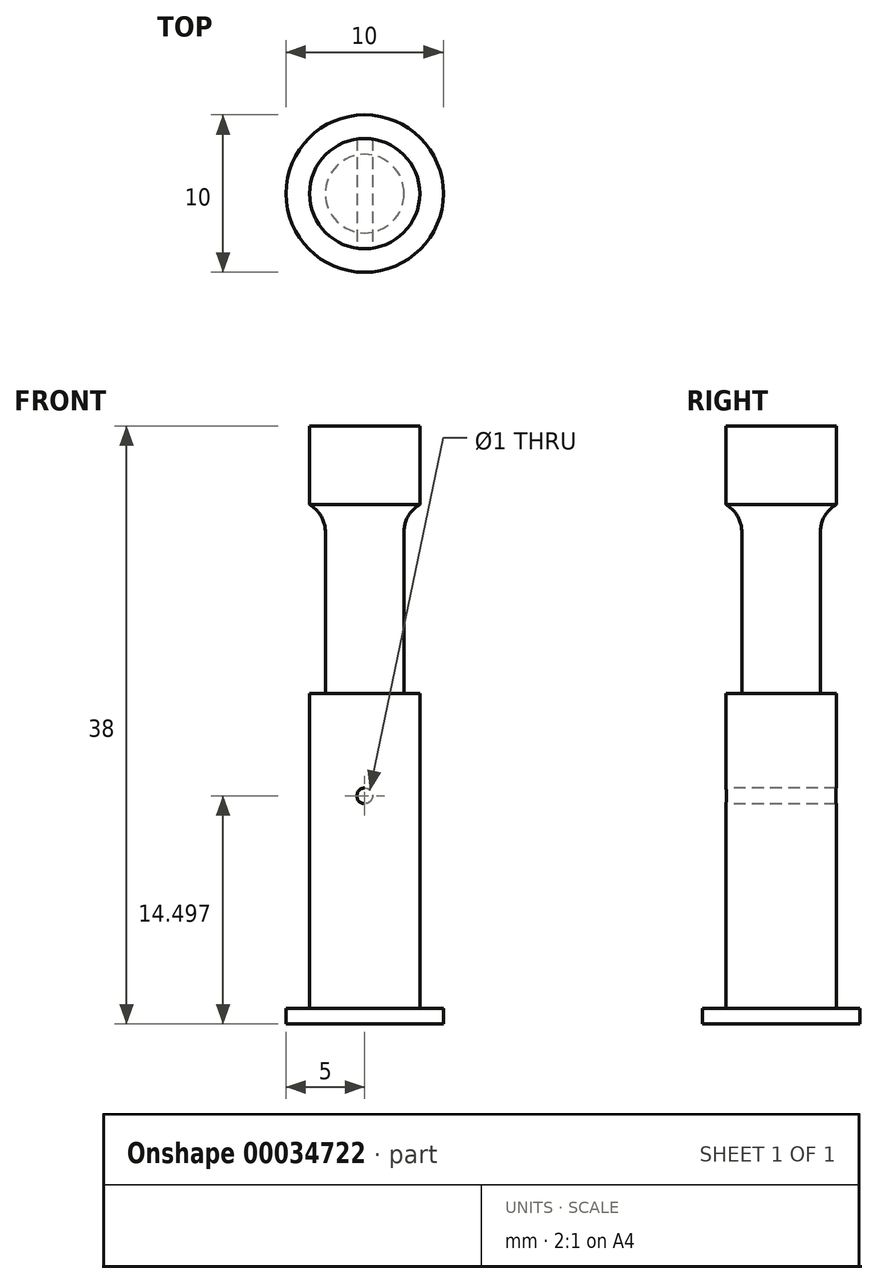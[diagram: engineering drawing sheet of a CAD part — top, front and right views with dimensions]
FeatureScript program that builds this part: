
annotation { "Feature Type Name" : "Feature", "Feature Type Description" : "" }
export const myFeature = defineFeature(function(context is Context, id is Id, definition is map)
    precondition{}
    {
        {
            var Q0;
            Q0=qCreatedBy(makeId("Top.planeOp"),FACE);
            var sketch = newSketch(context, id + "F0", { "sketchPlane" : qUnion([Q0])});
            skCircle(sketch, "E0", {"center": v(0, 0) * mm, "radius": 3.5 * mm});
            skCircle(sketch, "E1", {"center": v(0, 0) * mm, "radius": 5 * mm});
            skSolve(sketch);
        }
        {
            var Q0;
            Q0=makeQuery(id+"F0.imprint","IMPRINT",FACE,{"disambiguationData":[TD([[makeQuery(id+"F0.imprint","IMPRINT",EDGE,{"derivedFrom":sQuery(id+"F0.wireOp",EDGE,"E0")}),1.0]])]});
            extrude(context, id + "F1", {"entities" : qUnion([Q0]), "depth" : 13 * mm});
        }
        {
            var Q0;
            Q0=makeQuery(id+"F1.opExtrude","CAP_FACE",FACE,{"disambiguationData":[OSD([sQuery(id+"F0.wireOp",EDGE,"E0")])],"isStart":false});
            var sketch = newSketch(context, id + "F7", { "sketchPlane" : qUnion([Q0])});
            skCircle(sketch, "E2", {"center": v(0, 0) * mm, "radius": 3.5 * mm});
            skCircle(sketch, "E3", {"center": v(0, 0) * mm, "radius": 2.5 * mm});
            skSolve(sketch);
        }
        {
            var Q0;
            Q0=makeQuery(id+"F7.imprint","IMPRINT",FACE,{"disambiguationData":[TD([[makeQuery(id+"F7.imprint","IMPRINT",EDGE,{"derivedFrom":sQuery(id+"F7.wireOp",EDGE,"E2")}),1.0]])]});
            var Q1;
            Q1=makeQuery(id+"F7.imprint","IMPRINT",FACE,{"disambiguationData":[TD([[makeQuery(id+"F7.imprint","IMPRINT",EDGE,{"derivedFrom":sQuery(id+"F7.wireOp",EDGE,"E3")}),1.0]])]});
            extrude(context, id + "F8", {"entities" : qUnion([Q0, Q1]), "operationType" : NewBodyOperationType.ADD, "depth" : 25 * mm});
        }
        {
            var Q0;
            Q0=makeQuery(id+"F7.imprint","IMPRINT",FACE,{"disambiguationData":[TD([[makeQuery(id+"F7.imprint","IMPRINT",EDGE,{"derivedFrom":sQuery(id+"F7.wireOp",EDGE,"E2")}),1.0]])]});
            extrude(context, id + "F9", {"entities" : qUnion([Q0]), "operationType" : NewBodyOperationType.REMOVE, "depth" : 20 * mm, "hasSecondDirection" : true, "secondDirectionOppositeDirection" : false, "secondDirectionDepth" : 8 * mm});
        }
        {
            var Q0;
            Q0=makeQuery(id+"F9.boolean.opBoolean","COPY",EDGE,{"derivedFrom":makeQuery(id+"F9.opExtrude","CAP_EDGE",EDGE,{"disambiguationData":[OSD([sQuery(id+"F7.wireOp",EDGE,"E3")])],"isStart":false})});
            fillet(context, id + "F2", {"entities" : qUnion([Q0]), "radius" : 2 * mm, "tangentPropagation" : true, "allowEdgeOverflow" : false});
        }
        {
            var Q0;
            Q0=makeQuery(id+"F0.imprint","IMPRINT",FACE,{"disambiguationData":[TD([[makeQuery(id+"F0.imprint","IMPRINT",EDGE,{"derivedFrom":sQuery(id+"F0.wireOp",EDGE,"E0")}),-1.0]])]});
            extrude(context, id + "F3", {"entities" : qUnion([Q0]), "operationType" : NewBodyOperationType.ADD, "depth" : 1 * mm});
        }
        {
            var Q0;
            Q0=qCreatedBy(makeId("Front.planeOp"),FACE);
            var sketch = newSketch(context, id + "F4", { "sketchPlane" : qUnion([Q0])});
            skLineSegment(sketch, "E4", {"start": v(-3.5, 1) * mm, "end": v(-3.5, 21) * mm});
            skLineSegment(sketch, "E5", {"start": v(3.5, 21) * mm, "end": v(3.5, 1) * mm});
            skLineSegment(sketch, "E6", {"start": v(0, 21.1) * mm, "end": v(0, 0) * mm});
            skLineSegment(sketch, "E7", {"start": v(0, -0.3) * mm, "end": v(0, 14.5) * mm});
            skSolve(sketch);
        }
        {
            var Q0;
            Q0=sQuery(id+"F4.wireOp",VERTEX,"E7.end");
            var Q1;
            Q1=makeQuery(id+"F1.opExtrude","SWEPT_BODY",BODY,{"disambiguationData":[OSD([sQuery(id+"F0.wireOp",EDGE,"E0")])]});
            hole(context, id + "F5", {"style" : HoleStyle.SIMPLE, "endStyle" : HoleEndStyle.THROUGH, "holeDiameter" : 1 * mm, "majorDiameter" : 5 * mm, "isTappedThrough" : true, "tappedDepth" : 12 * mm, "tapClearance" : 3, "locations" : qUnion([Q0]), "scope" : qUnion([Q1])});
        }
        {
            var Q0;
            Q0=sQuery(id+"F4.wireOp",VERTEX,"E7.end");
            var Q1;
            Q1=makeQuery(id+"F1.opExtrude","SWEPT_BODY",BODY,{"disambiguationData":[OSD([sQuery(id+"F0.wireOp",EDGE,"E0")])]});
            hole(context, id + "F6", {"style" : HoleStyle.SIMPLE, "endStyle" : HoleEndStyle.BLIND, "oppositeDirection" : true, "holeDiameter" : 1 * mm, "majorDiameter" : 5 * mm, "holeDepth" : 12 * mm, "isTappedThrough" : true, "tappedDepth" : 12 * mm, "tapClearance" : 3, "locations" : qUnion([Q0]), "scope" : qUnion([Q1])});
        }
    });
